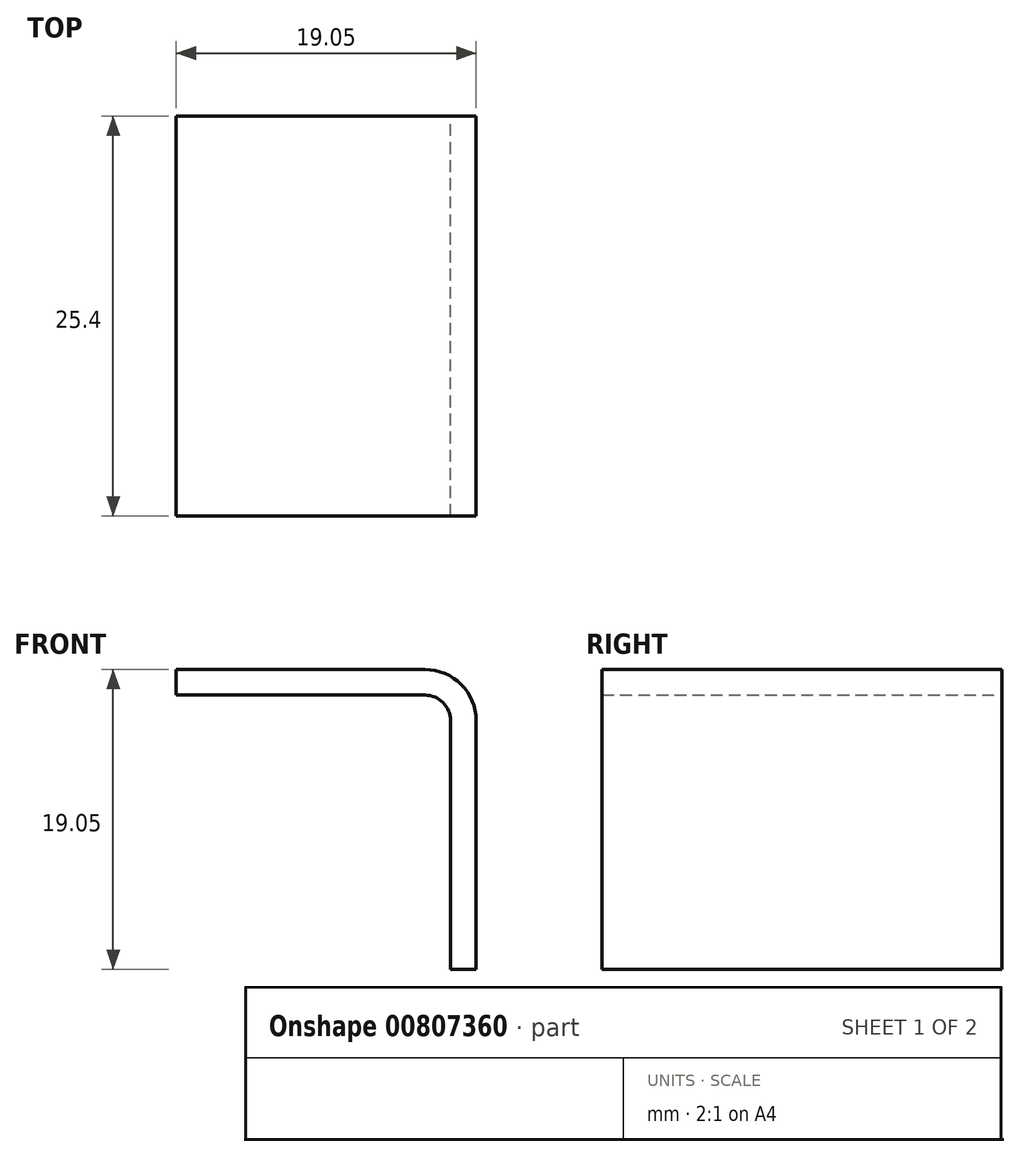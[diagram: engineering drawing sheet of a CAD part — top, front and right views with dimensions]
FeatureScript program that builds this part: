
annotation { "Feature Type Name" : "Feature", "Feature Type Description" : "" }
export const myFeature = defineFeature(function(context is Context, id is Id, definition is map)
    precondition{}
    {
        {
            var Q0;
            Q0=qCreatedBy(makeId("Front.planeOp"),FACE);
            var sketch = newSketch(context, id + "F0", { "sketchPlane" : qUnion([Q0])});
            skLineSegment(sketch, "E0", {"start": v(0, 0) * mm, "end": v(0, 19.05) * mm});
            skLineSegment(sketch, "E1", {"start": v(0, 19.05) * mm, "end": v(-19.05, 19.05) * mm});
            skLineSegment(sketch, "E2", {"start": v(-19.05, 19.05) * mm, "end": v(-19.05, 17.42) * mm});
            skLineSegment(sketch, "E3", {"start": v(-19.05, 17.42) * mm, "end": v(-1.63, 17.42) * mm});
            skLineSegment(sketch, "E4", {"start": v(-1.63, 17.42) * mm, "end": v(-1.63, 0) * mm});
            skLineSegment(sketch, "E5", {"start": v(-1.63, 0) * mm, "end": v(0, 0) * mm});
            skSolve(sketch);
        }
        {
            var Q0;
            Q0 = qSketchRegion(id + "F0", true);
            extrude(context, id + "F1", {"entities" : qUnion([Q0]), "depth" : 25.4 * mm, "offsetDistance" : 25.4 * mm});
        }
        {
            var Q0;
            Q0=makeQuery(id+"F1.opExtrude","SWEPT_EDGE",EDGE,{"disambiguationData":[OSD([sQuery(id+"F0.wireOp",EDGE,"E3"),sQuery(id+"F0.wireOp",EDGE,"E4")])]});
            fillet(context, id + "F2", {"entities" : qUnion([Q0]), "radius" : 1.63 * mm, "tangentPropagation" : true, "allowEdgeOverflow" : false});
        }
        {
            var Q0;
            Q0=makeQuery(id+"F1.opExtrude","SWEPT_EDGE",EDGE,{"disambiguationData":[OSD([sQuery(id+"F0.wireOp",EDGE,"E0"),sQuery(id+"F0.wireOp",EDGE,"E1")])]});
            fillet(context, id + "F3", {"entities" : qUnion([Q0]), "radius" : 3.25 * mm, "tangentPropagation" : true, "allowEdgeOverflow" : false});
        }
    });
